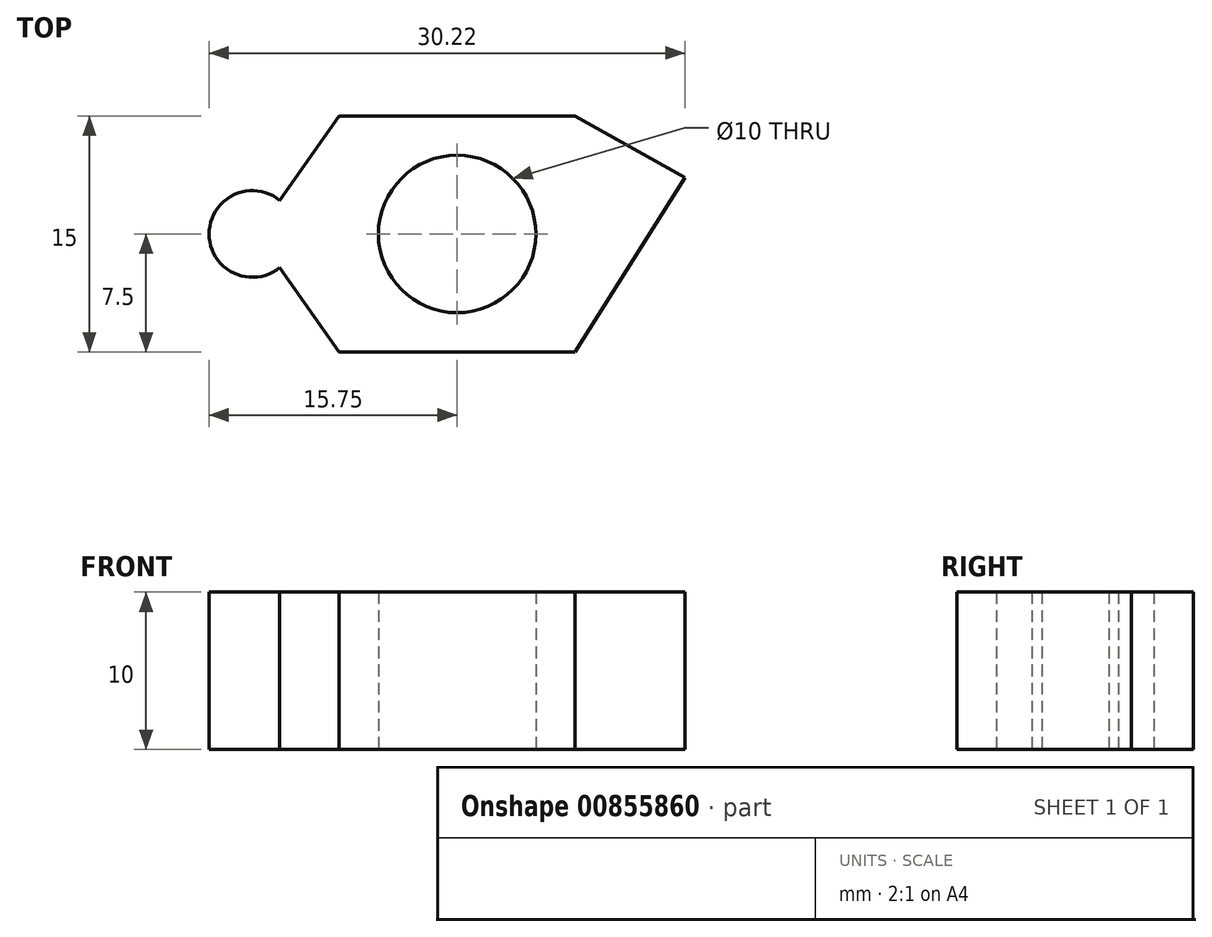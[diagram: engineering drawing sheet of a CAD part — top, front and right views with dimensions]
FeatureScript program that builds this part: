
annotation { "Feature Type Name" : "Feature", "Feature Type Description" : "" }
export const myFeature = defineFeature(function(context is Context, id is Id, definition is map)
    precondition{}
    {
        {
            var Q0;
            Q0=qCreatedBy(makeId("Top.planeOp"),FACE);
            var sketch = newSketch(context, id + "F0", { "sketchPlane" : qUnion([Q0])});
            skLineSegment(sketch, "E0.bottom", {"start": v(7.5, 7.5) * mm, "end": v(-7.5, 7.5) * mm});
            skLineSegment(sketch, "E0.top", {"start": v(7.5, -7.5) * mm, "end": v(-7.5, -7.5) * mm});
            skLineSegment(sketch, "E0.left", {"start": v(7.5, 7.5) * mm, "end": v(7.5, -7.5) * mm});
            skLineSegment(sketch, "E0.right", {"start": v(-7.5, 7.5) * mm, "end": v(-7.5, -7.5) * mm});
            skPoint(sketch, "E0.middle", {"position": v(0, 0) * mm});
            skCircle(sketch, "E1", {"center": v(0, 0) * mm, "radius": 5 * mm});
            skSolve(sketch);
        }
        {
            var Q0;
            Q0=qSketchRegion(id+"F0",true);
            extrude(context, id + "F1", {"entities" : qUnion([Q0]), "endBound" : BoundingType.SYMMETRIC, "depth" : 10 * mm, "offsetDistance" : 25 * mm});
        }
        {
            var Q0;
            Q0=qCreatedBy(makeId("Top.planeOp"),FACE);
            var sketch = newSketch(context, id + "F2", { "sketchPlane" : qUnion([Q0])});
            skArc(sketch, "E2", {"start": v(-11.26, 2.13) * mm, "mid": v(-15.75, 0) * mm, "end": v(-11.26, -2.13) * mm});
            skLineSegment(sketch, "E3.0", {"start": v(-7.5, 7.5) * mm, "end": v(-7.5, -7.5) * mm});
            skLineSegment(sketch, "E4", {"start": v(-11.26, 2.13) * mm, "end": v(-7.5, 7.5) * mm});
            skLineSegment(sketch, "E5", {"start": v(-11.26, -2.13) * mm, "end": v(-7.5, -7.5) * mm});
            skSolve(sketch);
        }
        {
            var Q0;
            Q0=qSketchRegion(id+"F2",true);
            extrude(context, id + "F3", {"entities" : qUnion([Q0]), "operationType" : NewBodyOperationType.ADD, "endBound" : BoundingType.SYMMETRIC, "depth" : 10 * mm, "offsetDistance" : 25 * mm});
        }
        {
            var Q0;
            Q0=qCreatedBy(makeId("Top.planeOp"),FACE);
            var sketch = newSketch(context, id + "F4", { "sketchPlane" : qUnion([Q0])});
            skLineSegment(sketch, "E6.0", {"start": v(7.5, 7.5) * mm, "end": v(7.5, -7.5) * mm});
            skLineSegment(sketch, "E7", {"start": v(7.5, -7.5) * mm, "end": v(14.47, 3.57) * mm});
            skLineSegment(sketch, "E8", {"start": v(14.47, 3.57) * mm, "end": v(7.5, 7.5) * mm});
            skSolve(sketch);
        }
        {
            var Q0;
            Q0 = qSketchRegion(id + "F4", true);
            extrude(context, id + "F5", {"entities" : qUnion([Q0]), "operationType" : NewBodyOperationType.ADD, "endBound" : BoundingType.SYMMETRIC, "depth" : 10 * mm, "offsetDistance" : 25 * mm});
        }
    });
